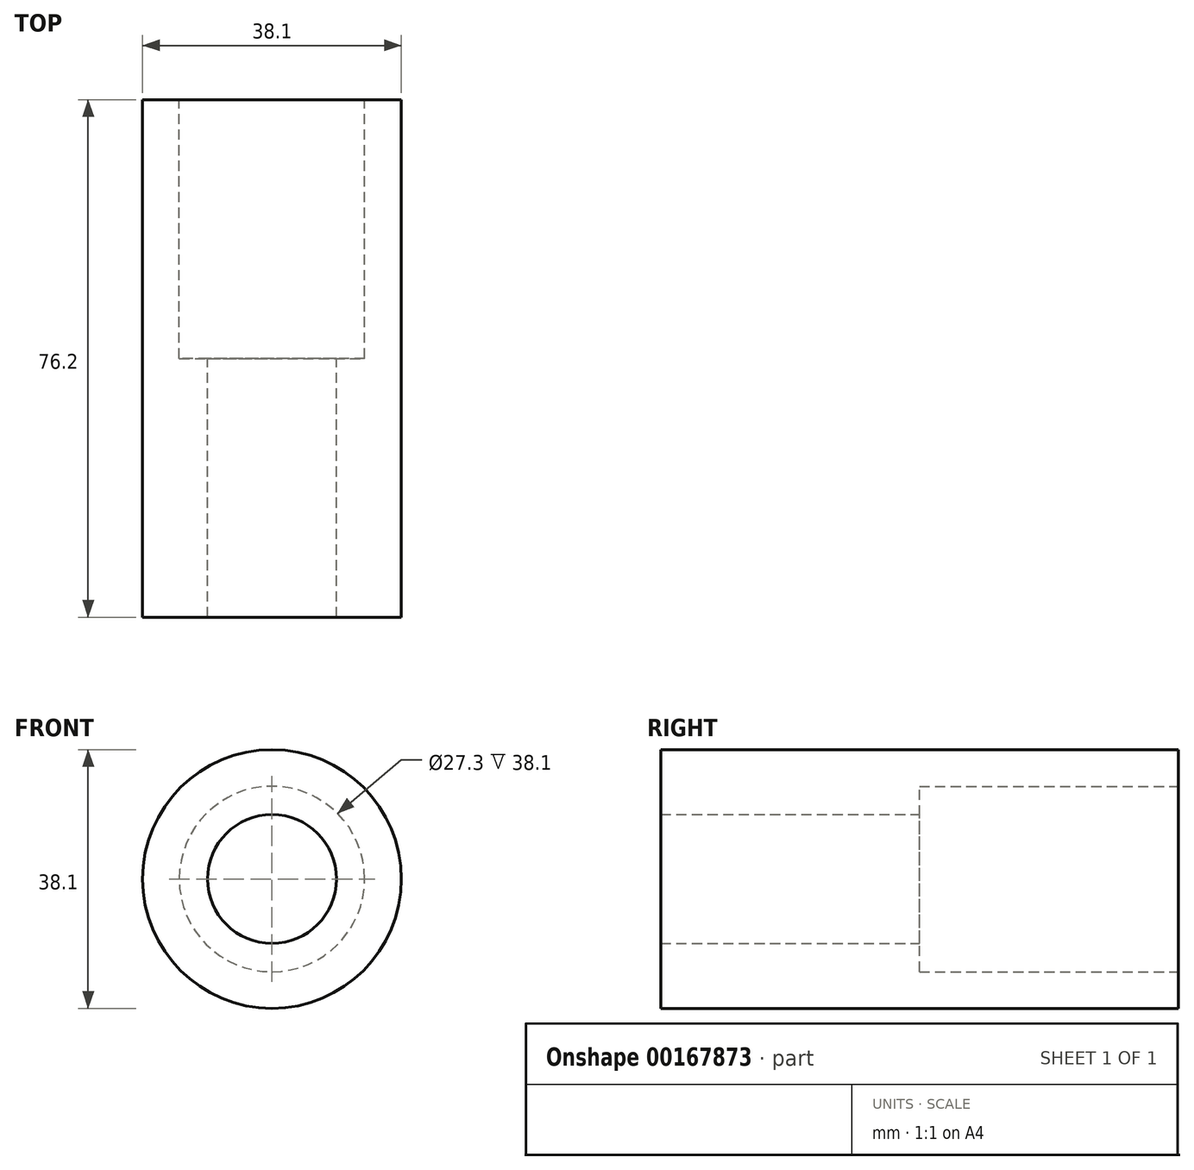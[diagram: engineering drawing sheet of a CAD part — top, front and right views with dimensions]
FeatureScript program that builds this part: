
annotation { "Feature Type Name" : "Feature", "Feature Type Description" : "" }
export const myFeature = defineFeature(function(context is Context, id is Id, definition is map)
    precondition{}
    {
        {
            var Q0;
            Q0=qCreatedBy(makeId("Front.planeOp"),FACE);
            var sketch = newSketch(context, id + "F0", { "sketchPlane" : qUnion([Q0])});
            skCircle(sketch, "E0", {"center": v(0, 0) * mm, "radius": 19.05 * mm});
            skCircle(sketch, "E1", {"center": v(0, 0) * mm, "radius": 9.5 * mm});
            skSolve(sketch);
        }
        {
            var Q0;
            Q0 = qSketchRegion(id + "F0", true);
            extrude(context, id + "F1", {"entities" : qUnion([Q0]), "depth" : 76.2 * mm});
        }
        {
            var Q0;
            Q0=qCreatedBy(makeId("Front.planeOp"),FACE);
            var sketch = newSketch(context, id + "F2", { "sketchPlane" : qUnion([Q0])});
            skCircle(sketch, "E2", {"center": v(0, 0) * mm, "radius": 13.65 * mm});
            skSolve(sketch);
        }
        {
            var Q0;
            Q0=makeQuery(id+"F2.imprint","IMPRINT",FACE,{"disambiguationData":[TD([[makeQuery(id+"F2.imprint","IMPRINT",EDGE,{"derivedFrom":sQuery(id+"F2.wireOp",EDGE,"E2")}),1.0]])]});
            extrude(context, id + "F3", {"entities" : qUnion([Q0]), "operationType" : NewBodyOperationType.REMOVE, "depth" : 38.1 * mm});
        }
    });
